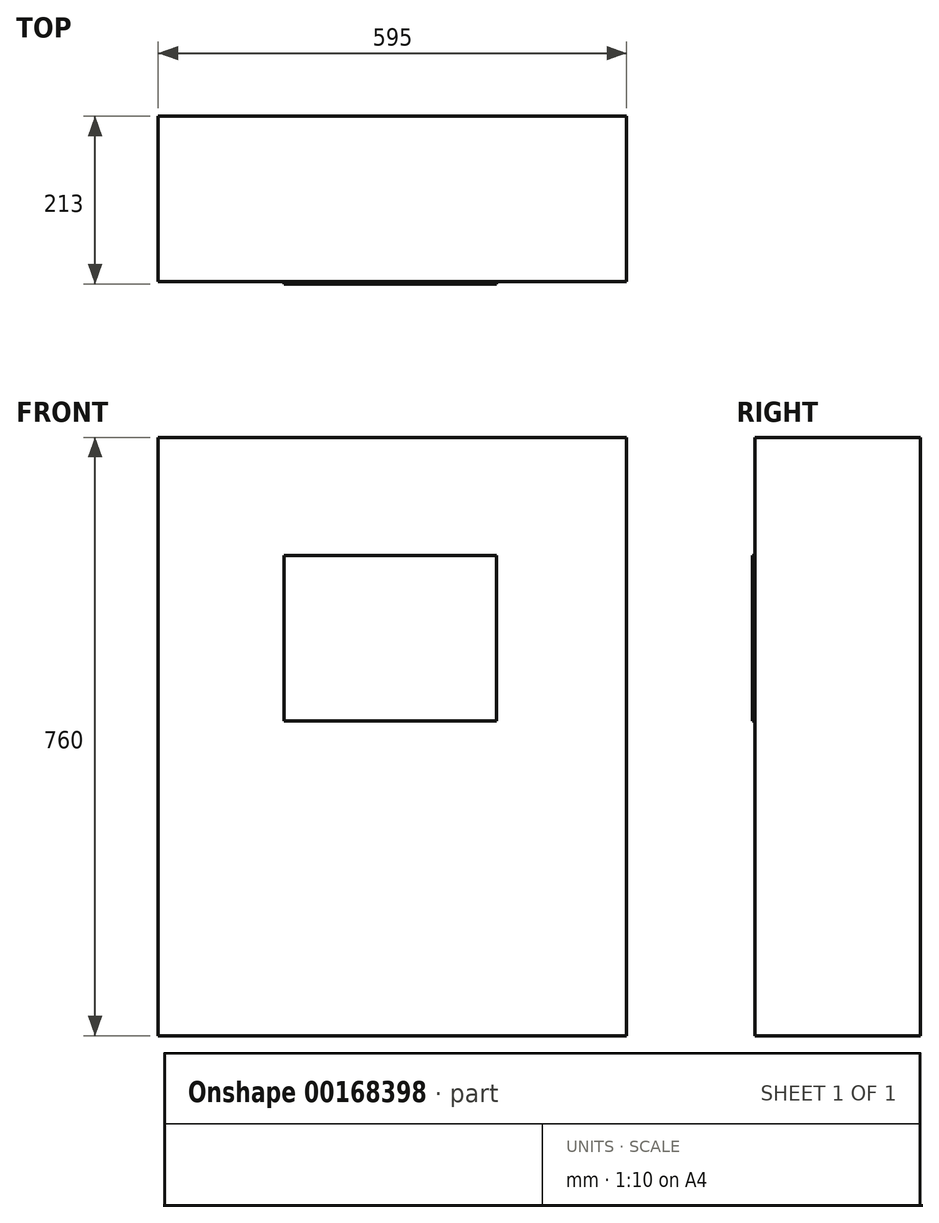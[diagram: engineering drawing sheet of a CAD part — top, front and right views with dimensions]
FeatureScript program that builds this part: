
annotation { "Feature Type Name" : "Feature", "Feature Type Description" : "" }
export const myFeature = defineFeature(function(context is Context, id is Id, definition is map)
    precondition{}
    {
        {
            var Q0;
            Q0=qCreatedBy(makeId("Front.planeOp"),FACE);
            var sketch = newSketch(context, id + "F0", { "sketchPlane" : qUnion([Q0])});
            skLineSegment(sketch, "E0.bottom", {"start": v(297.5, 380) * mm, "end": v(-297.5, 380) * mm});
            skLineSegment(sketch, "E0.top", {"start": v(297.5, -380) * mm, "end": v(-297.5, -380) * mm});
            skLineSegment(sketch, "E0.left", {"start": v(297.5, 380) * mm, "end": v(297.5, -380) * mm});
            skLineSegment(sketch, "E0.right", {"start": v(-297.5, 380) * mm, "end": v(-297.5, -380) * mm});
            skPoint(sketch, "E0.middle", {"position": v(0, 0) * mm});
            skSolve(sketch);
        }
        {
            var Q0;
            Q0=makeQuery(id+"F0.imprint","IMPRINT",FACE,{"disambiguationData":[TD([[makeQuery(id+"F0.imprint","IMPRINT",EDGE,{"derivedFrom":sQuery(id+"F0.wireOp",EDGE,"E0.bottom")}),1.0]])]});
            extrude(context, id + "F1", {"entities" : qUnion([Q0]), "oppositeDirection" : true, "depth" : 210 * mm});
        }
        {
            var Q0;
            Q0=makeQuery(id+"F1.opExtrude","CAP_FACE",FACE,{"disambiguationData":[OSD([sQuery(id+"F0.wireOp",EDGE,"E0.bottom"),sQuery(id+"F0.wireOp",EDGE,"E0.top"),sQuery(id+"F0.wireOp",EDGE,"E0.left"),sQuery(id+"F0.wireOp",EDGE,"E0.right")])],"isStart":true});
            var sketch = newSketch(context, id + "F2", { "sketchPlane" : qUnion([Q0])});
            skLineSegment(sketch, "E1.bottom", {"start": v(-137.5, 20) * mm, "end": v(132.5, 20) * mm});
            skLineSegment(sketch, "E1.top", {"start": v(-137.5, 230) * mm, "end": v(132.5, 230) * mm});
            skLineSegment(sketch, "E1.left", {"start": v(-137.5, 20) * mm, "end": v(-137.5, 230) * mm});
            skLineSegment(sketch, "E1.right", {"start": v(132.5, 20) * mm, "end": v(132.5, 230) * mm});
            skLineSegment(sketch, "E2.0", {"start": v(297.5, 380) * mm, "end": v(-297.5, 380) * mm});
            skLineSegment(sketch, "E3.0", {"start": v(297.5, 380) * mm, "end": v(297.5, -380) * mm});
            skSolve(sketch);
        }
        {
            var Q0;
            Q0=makeQuery(id+"F2.imprint","IMPRINT",FACE,{"disambiguationData":[TD([[makeQuery(id+"F2.imprint","IMPRINT",EDGE,{"derivedFrom":sQuery(id+"F2.wireOp",EDGE,"E1.bottom")}),1.0]])]});
            extrude(context, id + "F3", {"entities" : qUnion([Q0]), "depth" : 3 * mm});
        }
    });
